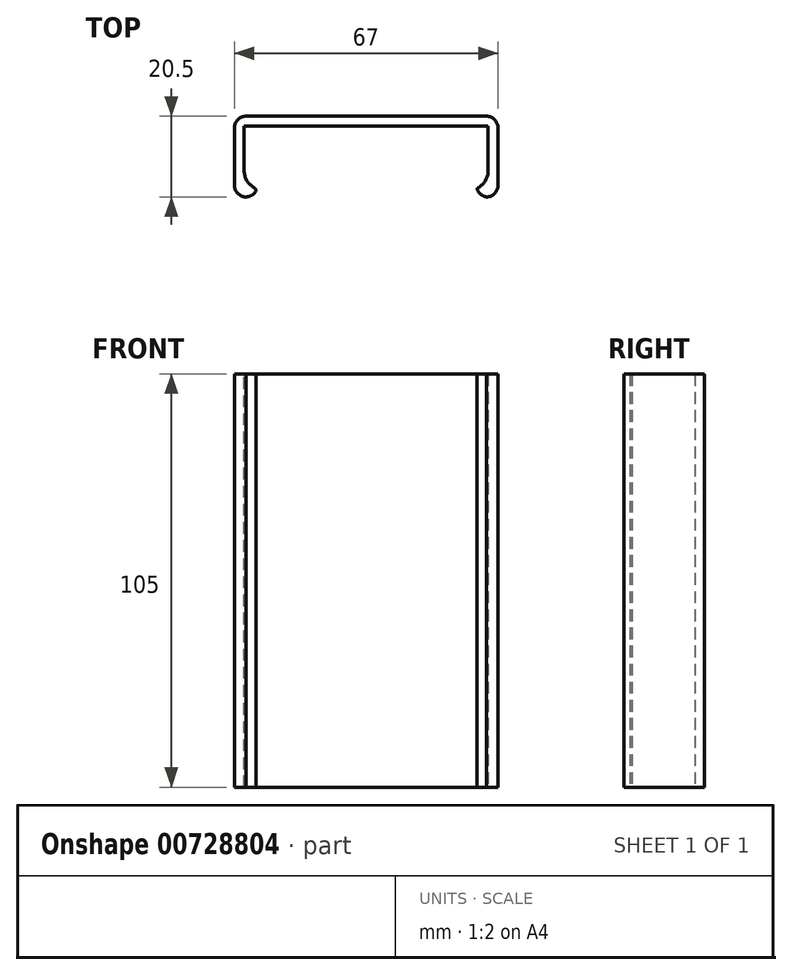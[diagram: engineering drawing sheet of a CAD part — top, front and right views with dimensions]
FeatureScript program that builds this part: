
annotation { "Feature Type Name" : "Feature", "Feature Type Description" : "" }
export const myFeature = defineFeature(function(context is Context, id is Id, definition is map)
    precondition{}
    {
        {
            var Q0;
            Q0=qCreatedBy(makeId("Top.planeOp"),FACE);
            var sketch = newSketch(context, id + "F0", { "sketchPlane" : qUnion([Q0])});
            skLineSegment(sketch, "E0", {"start": v(49.67, 0) * mm, "end": v(-17.33, 0) * mm});
            skLineSegment(sketch, "E1", {"start": v(-17.33, 0) * mm, "end": v(-17.33, -17.5) * mm});
            skLineSegment(sketch, "E2", {"start": v(-14.33, -20.5) * mm, "end": v(-11.83, -20.5) * mm});
            skLineSegment(sketch, "E3", {"start": v(-11.83, -20.5) * mm, "end": v(-11.83, -19) * mm});
            skLineSegment(sketch, "E4", {"start": v(-12.83, -18) * mm, "end": v(-14.83, -18) * mm});
            skLineSegment(sketch, "E5", {"start": v(-14.83, -18) * mm, "end": v(-14.83, -2.5) * mm});
            skLineSegment(sketch, "E6", {"start": v(-14.83, -2.5) * mm, "end": v(47.17, -2.5) * mm});
            skLineSegment(sketch, "E7", {"start": v(47.17, -2.5) * mm, "end": v(47.17, -18) * mm});
            skLineSegment(sketch, "E8", {"start": v(47.17, -18) * mm, "end": v(45.17, -18) * mm});
            skLineSegment(sketch, "E9", {"start": v(44.17, -19) * mm, "end": v(44.17, -20.5) * mm});
            skLineSegment(sketch, "E10", {"start": v(44.17, -20.5) * mm, "end": v(46.67, -20.5) * mm});
            skLineSegment(sketch, "E11", {"start": v(49.67, -17.5) * mm, "end": v(49.67, 0) * mm});
            skPoint(sketch, "E12.visualSharp", {"position": v(-17.33, 0) * mm});
            skLineSegment(sketch, "E12.filletArc", {"start": v(-17.33, 0) * mm, "end": v(-17.33, 0) * mm});
            skPoint(sketch, "E13.visualSharp", {"position": v(49.67, 0) * mm});
            skLineSegment(sketch, "E13.filletArc", {"start": v(49.67, 0) * mm, "end": v(49.67, 0) * mm});
            skLineSegment(sketch, "E14.filletArc", {"start": v(-14.83, -2.5) * mm, "end": v(-14.83, -2.5) * mm});
            skPoint(sketch, "E15.visualSharp", {"position": v(47.17, -2.5) * mm});
            skLineSegment(sketch, "E15.filletArc", {"start": v(47.17, -2.5) * mm, "end": v(47.17, -2.5) * mm});
            skPoint(sketch, "E16.visualSharp", {"position": v(-11.83, -18) * mm});
            skArc(sketch, "E16.filletArc", {"start": v(-11.83, -19) * mm, "mid": v(-12.12, -18.3) * mm, "end": v(-12.83, -18) * mm});
            skPoint(sketch, "E17.visualSharp", {"position": v(44.17, -18) * mm});
            skArc(sketch, "E17.filletArc", {"start": v(45.17, -18) * mm, "mid": v(44.47, -18.3) * mm, "end": v(44.17, -19) * mm});
            skPoint(sketch, "E18.visualSharp", {"position": v(49.67, -20.5) * mm});
            skArc(sketch, "E18.filletArc", {"start": v(46.67, -20.5) * mm, "mid": v(48.8, -19.62) * mm, "end": v(49.67, -17.5) * mm});
            skPoint(sketch, "E19.visualSharp", {"position": v(-17.33, -20.5) * mm});
            skArc(sketch, "E19.filletArc", {"start": v(-17.33, -17.5) * mm, "mid": v(-16.45, -19.62) * mm, "end": v(-14.33, -20.5) * mm});
            skSolve(sketch);
        }
        {
            var Q0;
            Q0=makeQuery(id+"F0.imprint","IMPRINT",FACE,{"disambiguationData":[TD([[makeQuery(id+"F0.imprint","IMPRINT",EDGE,{"derivedFrom":sQuery(id+"F0.wireOp",EDGE,"E0")}),1.0]])]});
            extrude(context, id + "F1", {"entities" : qUnion([Q0]), "depth" : 105 * mm, "offsetDistance" : 25 * mm});
        }
        {
            var Q0;
            Q0=makeQuery(id+"F1.opExtrude","SWEPT_EDGE",EDGE,{"disambiguationData":[OSD([sQuery(id+"F0.wireOp",EDGE,"E0"),sQuery(id+"F0.wireOp",EDGE,"E11")])]});
            var Q1;
            Q1=makeQuery(id+"F1.opExtrude","SWEPT_EDGE",EDGE,{"disambiguationData":[OSD([sQuery(id+"F0.wireOp",EDGE,"E0"),sQuery(id+"F0.wireOp",EDGE,"E1")])]});
            fillet(context, id + "F2", {"entities" : qUnion([Q0, Q1]), "radius" : 3 * mm, "tangentPropagation" : true, "allowEdgeOverflow" : false});
        }
        {
            var Q0;
            Q0=makeQuery(id+"F1.opExtrude","SWEPT_EDGE",EDGE,{"disambiguationData":[OSD([sQuery(id+"F0.wireOp",EDGE,"E9"),sQuery(id+"F0.wireOp",EDGE,"E10")])]});
            var Q1;
            Q1=makeQuery(id+"F1.opExtrude","SWEPT_EDGE",EDGE,{"disambiguationData":[OSD([sQuery(id+"F0.wireOp",EDGE,"E2"),sQuery(id+"F0.wireOp",EDGE,"E3")])]});
            fillet(context, id + "F3", {"entities" : qUnion([Q0, Q1]), "radius" : 3 * mm, "tangentPropagation" : true, "allowEdgeOverflow" : false});
        }
        {
            var Q0;
            Q0=makeQuery(id+"F1.opExtrude","SWEPT_EDGE",EDGE,{"disambiguationData":[OSD([sQuery(id+"F0.wireOp",EDGE,"E7"),sQuery(id+"F0.wireOp",EDGE,"E8")])]});
            var Q1;
            Q1=makeQuery(id+"F1.opExtrude","SWEPT_EDGE",EDGE,{"disambiguationData":[OSD([sQuery(id+"F0.wireOp",EDGE,"E4"),sQuery(id+"F0.wireOp",EDGE,"E5")])]});
            fillet(context, id + "F4", {"entities" : qUnion([Q0, Q1]), "radius" : 5 * mm, "tangentPropagation" : true, "allowEdgeOverflow" : false});
        }
    });
